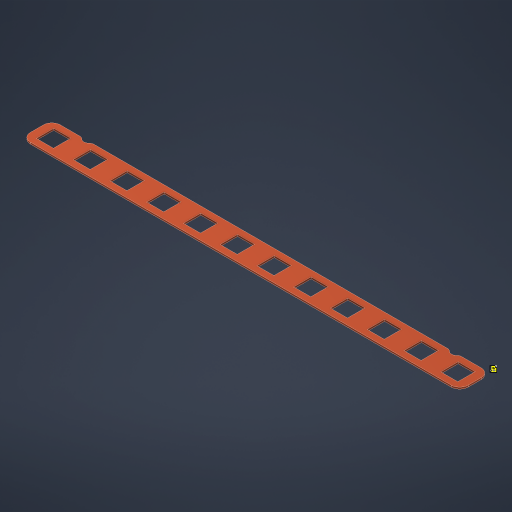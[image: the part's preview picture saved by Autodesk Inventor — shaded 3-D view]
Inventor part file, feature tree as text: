
AUTODESK INVENTOR PART (.ipt)
format: ipt  version: 2024.3 (Build 283343010, 343A)  size: 351,232 bytes
history: native  units: mm
features: fillet x2, sketch x2, extrude x1, projected_geometry x1
ambient origin geometry x8: Origin, YZ Plane, XZ Plane, XY Plane, X Axis, Y Axis, Z Axis, Center Point
bodies: Volumenkörper1 (feature_tree)
feature tree (6):
  extrude  "Extrusion1"  Depth=17.5mm
  fillet  "Rundung1"  Radius=10.2mm
  fillet  "Rundung2"  Radius=10.0mm
  sketch  "Skizze2"  dims[d14=1.0mm d15=0.0mm d16=5.0mm d17=120.0mm d19=21.5mm d20=10.0mm d22=10.0mm d24=43.0mm d25=21.5mm d26=10.75mm d32=3.0mm d33=1.25mm d34=10.75mm d35=10.75mm d36=3.0mm]
  sketch  "Skizze1"  dims[d0=256.0mm d1=17.5mm d2=10.2mm d3=10.0mm]
  projected_geometry  "Projizierte Kontur1"
